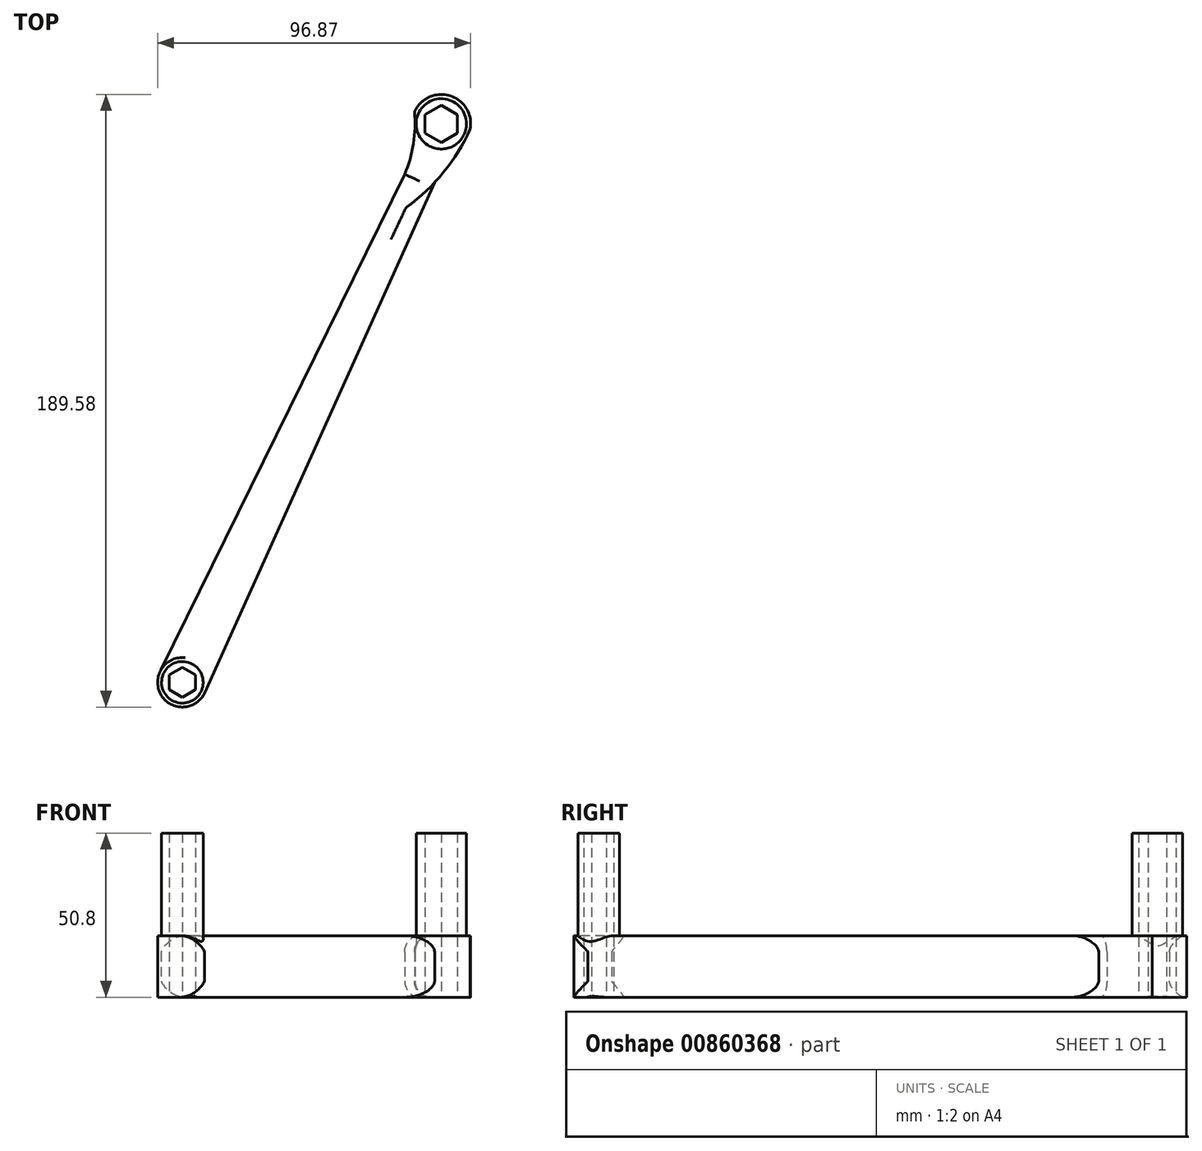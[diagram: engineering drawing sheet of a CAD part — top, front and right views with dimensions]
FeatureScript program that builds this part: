
annotation { "Feature Type Name" : "Feature", "Feature Type Description" : "" }
export const myFeature = defineFeature(function(context is Context, id is Id, definition is map)
    precondition{}
    {
        {
            var Q0;
            Q0=qCreatedBy(makeId("Top.planeOp"),FACE);
            var sketch = newSketch(context, id + "F0", { "sketchPlane" : qUnion([Q0])});
            skCircle(sketch, "E0.cCircle", {"center": v(0, 0) * mm, "radius": 5.77 * mm, "construction": true});
            skLineSegment(sketch, "E0.0", {"start": v(0, 5.77) * mm, "end": v(5, 2.89) * mm});
            skLineSegment(sketch, "E0.1", {"start": v(5, 2.89) * mm, "end": v(5, -2.89) * mm});
            skLineSegment(sketch, "E0.2", {"start": v(5, -2.89) * mm, "end": v(0, -5.77) * mm});
            skLineSegment(sketch, "E0.3", {"start": v(0, -5.77) * mm, "end": v(-5, -2.89) * mm});
            skLineSegment(sketch, "E0.4", {"start": v(-5, -2.89) * mm, "end": v(-5, 2.89) * mm});
            skLineSegment(sketch, "E0.5", {"start": v(-5, 2.89) * mm, "end": v(0, 5.77) * mm});
            skArc(sketch, "E1", {"start": v(8.94, -1.64) * mm, "mid": v(2.7, 8.68) * mm, "end": v(-8.3, 3.73) * mm});
            skCircle(sketch, "E2.cCircle", {"center": v(-80.12, -172.83) * mm, "radius": 4.62 * mm, "construction": true});
            skLineSegment(sketch, "E2.0", {"start": v(-80.12, -168.21) * mm, "end": v(-76.12, -170.52) * mm});
            skLineSegment(sketch, "E2.1", {"start": v(-76.12, -170.52) * mm, "end": v(-76.12, -175.14) * mm});
            skLineSegment(sketch, "E2.2", {"start": v(-76.12, -175.14) * mm, "end": v(-80.12, -177.45) * mm});
            skLineSegment(sketch, "E2.3", {"start": v(-80.12, -177.45) * mm, "end": v(-84.12, -175.14) * mm});
            skLineSegment(sketch, "E2.4", {"start": v(-84.12, -175.14) * mm, "end": v(-84.12, -170.52) * mm});
            skLineSegment(sketch, "E2.5", {"start": v(-84.12, -170.52) * mm, "end": v(-80.12, -168.21) * mm});
            skArc(sketch, "E3", {"start": v(-86.67, -168.85) * mm, "mid": v(-83.6, -179.66) * mm, "end": v(-73.05, -175.78) * mm});
            skLineSegment(sketch, "E4", {"start": v(-86.67, -168.85) * mm, "end": v(-11.33, -15.62) * mm});
            skLineSegment(sketch, "E5", {"start": v(-73.23, -176.17) * mm, "end": v(-2.08, -18.16) * mm});
            skArc(sketch, "E6", {"start": v(-11.33, -15.62) * mm, "mid": v(-8.64, -6.13) * mm, "end": v(-8.3, 3.73) * mm});
            skArc(sketch, "E7", {"start": v(-2.08, -18.16) * mm, "mid": v(4.11, -10.35) * mm, "end": v(8.94, -1.64) * mm});
            skPoint(sketch, "E8", {"position": v(2.7, 8.68) * mm});
            skPoint(sketch, "E9", {"position": v(-83.6, -179.66) * mm});
            skSolve(sketch);
        }
        {
            var Q0;
            {var subQ0=sQuery(id+"F0.wireOp",EDGE,"E5");var subQ1=sQuery(id+"F0.wireOp",EDGE,"E3");var subQ2=makeQuery(id+"F0.imprint","INTERSECT",VERTEX,{"disambiguationData":[OD(0.0)],"derivedFrom":[subQ1,subQ0]});Q0=makeQuery(id+"F0.imprint","IMPRINT",FACE,{"disambiguationData":[TD([[makeQuery(id+"F0.imprint","IMPRINT",EDGE,{"disambiguationData":[TD([[subQ2,1.0]])],"derivedFrom":subQ1}),1.0]])]});}
            var Q1;
            Q1=makeQuery(id+"F0.imprint","IMPRINT",FACE,{"disambiguationData":[TD([[makeQuery(id+"F0.imprint","IMPRINT",EDGE,{"derivedFrom":sQuery(id+"F0.wireOp",EDGE,"E0.0")}),1.0]])]});
            extrude(context, id + "F1", {"entities" : qUnion([Q0, Q1]), "depth" : 19.05 * mm, "offsetDistance" : 25.4 * mm});
        }
        {
            var Q0;
            Q0=makeQuery(id+"F1.opExtrude","CAP_FACE",FACE,{"disambiguationData":[OSD([sQuery(id+"F0.wireOp",EDGE,"E0.0"),sQuery(id+"F0.wireOp",EDGE,"E0.1"),sQuery(id+"F0.wireOp",EDGE,"E0.2"),sQuery(id+"F0.wireOp",EDGE,"E0.3"),sQuery(id+"F0.wireOp",EDGE,"E0.4"),sQuery(id+"F0.wireOp",EDGE,"E0.5"),sQuery(id+"F0.wireOp",EDGE,"E1"),sQuery(id+"F0.wireOp",EDGE,"E2.0"),sQuery(id+"F0.wireOp",EDGE,"E2.1"),sQuery(id+"F0.wireOp",EDGE,"E2.2"),sQuery(id+"F0.wireOp",EDGE,"E2.3"),sQuery(id+"F0.wireOp",EDGE,"E2.4"),sQuery(id+"F0.wireOp",EDGE,"E2.5"),sQuery(id+"F0.wireOp",EDGE,"E3"),sQuery(id+"F0.wireOp",EDGE,"E4"),sQuery(id+"F0.wireOp",EDGE,"E5"),sQuery(id+"F0.wireOp",EDGE,"E6"),sQuery(id+"F0.wireOp",EDGE,"E7")])],"isStart":false});
            var sketch = newSketch(context, id + "F2", { "sketchPlane" : qUnion([Q0])});
            skCircle(sketch, "E10", {"center": v(0, 0) * mm, "radius": 7.8 * mm});
            skCircle(sketch, "E11", {"center": v(-80.12, -172.83) * mm, "radius": 6.44 * mm});
            skCircle(sketch, "E12.cCircle", {"center": v(-80.12, -172.83) * mm, "radius": 4.62 * mm, "construction": true});
            skLineSegment(sketch, "E12.0", {"start": v(-80.12, -168.21) * mm, "end": v(-76.12, -170.52) * mm});
            skLineSegment(sketch, "E12.1", {"start": v(-76.12, -170.52) * mm, "end": v(-76.12, -175.14) * mm});
            skLineSegment(sketch, "E12.2", {"start": v(-76.12, -175.14) * mm, "end": v(-80.12, -177.45) * mm});
            skLineSegment(sketch, "E12.3", {"start": v(-80.12, -177.45) * mm, "end": v(-84.12, -175.14) * mm});
            skLineSegment(sketch, "E12.4", {"start": v(-84.12, -175.14) * mm, "end": v(-84.12, -170.52) * mm});
            skLineSegment(sketch, "E12.5", {"start": v(-84.12, -170.52) * mm, "end": v(-80.12, -168.21) * mm});
            skCircle(sketch, "E13.cCircle", {"center": v(0, 0) * mm, "radius": 5.77 * mm, "construction": true});
            skLineSegment(sketch, "E13.0", {"start": v(0, 5.77) * mm, "end": v(5, 2.89) * mm});
            skLineSegment(sketch, "E13.1", {"start": v(5, 2.89) * mm, "end": v(5, -2.89) * mm});
            skLineSegment(sketch, "E13.2", {"start": v(5, -2.89) * mm, "end": v(0, -5.77) * mm});
            skLineSegment(sketch, "E13.3", {"start": v(0, -5.77) * mm, "end": v(-5, -2.89) * mm});
            skLineSegment(sketch, "E13.4", {"start": v(-5, -2.89) * mm, "end": v(-5, 2.89) * mm});
            skLineSegment(sketch, "E13.5", {"start": v(-5, 2.89) * mm, "end": v(0, 5.77) * mm});
            skSolve(sketch);
        }
        {
            var Q0;
            Q0 = qSketchRegion(id + "F2", true);
            extrude(context, id + "F3", {"entities" : qUnion([Q0]), "operationType" : NewBodyOperationType.ADD, "depth" : 31.75 * mm, "offsetDistance" : 25.4 * mm});
        }
        {
            var Q0;
            Q0=makeQuery(id+"F1.opExtrude","CAP_EDGE",EDGE,{"disambiguationData":[OSD([sQuery(id+"F0.wireOp",EDGE,"E5")])],"isStart":false});
            var Q1;
            Q1=makeQuery(id+"F1.opExtrude","CAP_EDGE",EDGE,{"disambiguationData":[OSD([sQuery(id+"F0.wireOp",EDGE,"E5")])],"isStart":true});
            var Q2;
            Q2=makeQuery(id+"F1.opExtrude","CAP_EDGE",EDGE,{"disambiguationData":[OSD([sQuery(id+"F0.wireOp",EDGE,"E4")])],"isStart":false});
            var Q3;
            Q3=makeQuery(id+"F1.opExtrude","CAP_EDGE",EDGE,{"disambiguationData":[OSD([sQuery(id+"F0.wireOp",EDGE,"E4")])],"isStart":true});
            fillet(context, id + "F4", {"entities" : qUnion([Q0, Q1, Q2, Q3]), "radius" : 5.08 * mm, "tangentPropagation" : true, "allowEdgeOverflow" : false});
        }
    });
